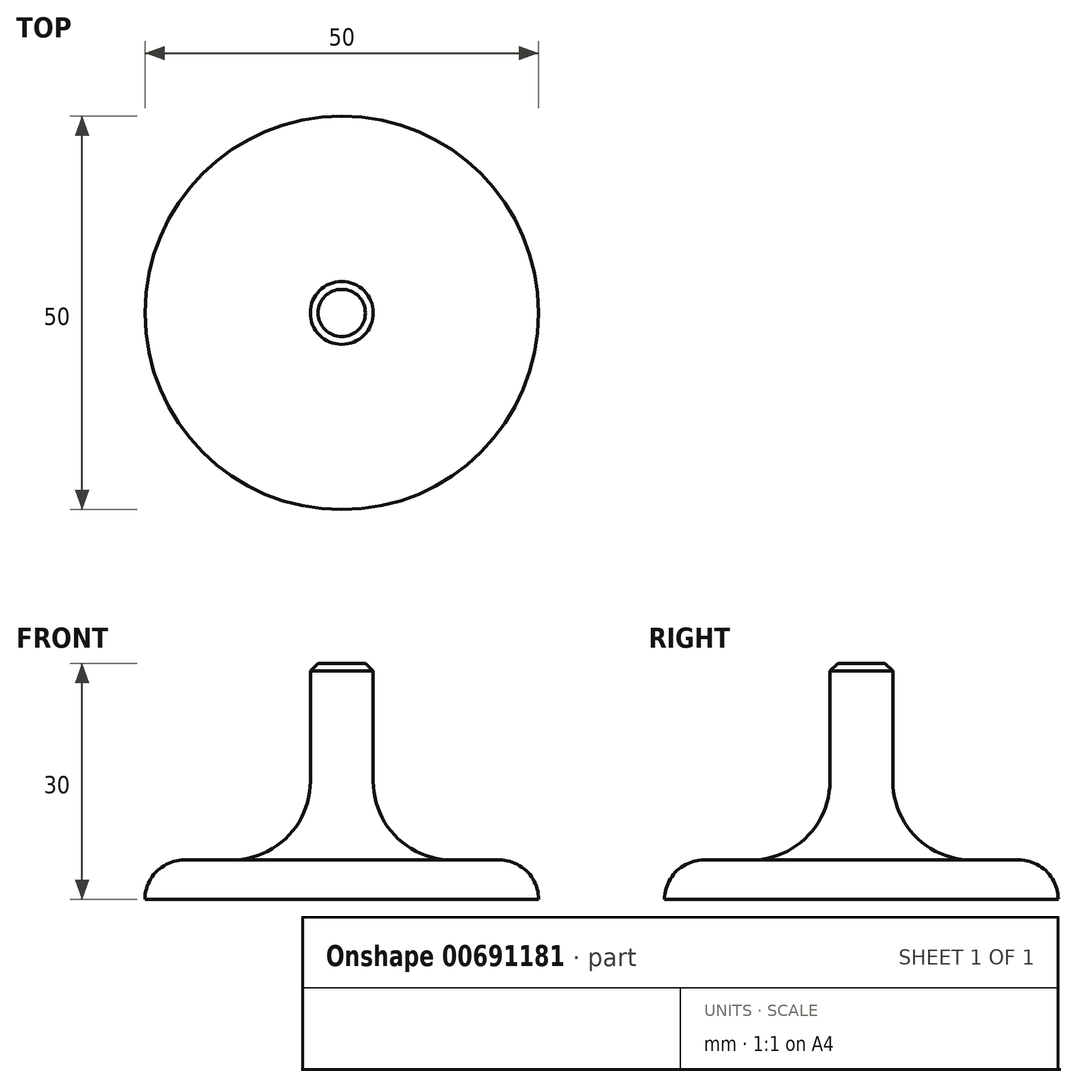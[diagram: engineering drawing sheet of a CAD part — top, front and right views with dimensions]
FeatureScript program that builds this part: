
annotation { "Feature Type Name" : "Feature", "Feature Type Description" : "" }
export const myFeature = defineFeature(function(context is Context, id is Id, definition is map)
    precondition{}
    {
        {
            var Q0;
            Q0=qCreatedBy(makeId("Top.planeOp"),FACE);
            var sketch = newSketch(context, id + "F0", { "sketchPlane" : qUnion([Q0])});
            skCircle(sketch, "E0", {"center": v(0, 0) * mm, "radius": 25 * mm});
            skSolve(sketch);
        }
        {
            var Q0;
            Q0=makeQuery(id+"F0.imprint","IMPRINT",FACE,{"disambiguationData":[TD([[makeQuery(id+"F0.imprint","IMPRINT",EDGE,{"derivedFrom":sQuery(id+"F0.wireOp",EDGE,"E0")}),1.0]])]});
            var sketch = newSketch(context, id + "F1", { "sketchPlane" : qUnion([Q0])});
            skCircle(sketch, "E1", {"center": v(0, 0) * mm, "radius": 4 * mm});
            skSolve(sketch);
        }
        {
            var Q0;
            Q0=makeQuery(id+"F0.imprint","IMPRINT",FACE,{"disambiguationData":[TD([[makeQuery(id+"F0.imprint","IMPRINT",EDGE,{"derivedFrom":sQuery(id+"F0.wireOp",EDGE,"E0")}),1.0]])]});
            extrude(context, id + "F2", {"entities" : qUnion([Q0]), "depth" : 5 * mm, "offsetDistance" : 25 * mm});
        }
        {
            var Q0;
            Q0=makeQuery(id+"F1.imprint","IMPRINT",FACE,{"disambiguationData":[TD([[makeQuery(id+"F1.imprint","IMPRINT",EDGE,{"derivedFrom":sQuery(id+"F1.wireOp",EDGE,"E1")}),1.0]])]});
            extrude(context, id + "F3", {"entities" : qUnion([Q0]), "operationType" : NewBodyOperationType.ADD, "depth" : 30 * mm, "offsetDistance" : 25 * mm});
        }
        {
            var Q0;
            Q0=makeQuery(id+"F3.boolean.opBoolean","INTERSECT",EDGE,{"derivedFrom":[makeQuery(id+"F2.opExtrude","CAP_FACE",FACE,{"disambiguationData":[OSD([sQuery(id+"F0.wireOp",EDGE,"E0")])],"isStart":false}),makeQuery(id+"F3.opExtrude","SWEPT_FACE",FACE,{"disambiguationData":[OSD([sQuery(id+"F1.wireOp",EDGE,"E1")])]})]});
            fillet(context, id + "F4", {"entities" : qUnion([Q0]), "radius" : 10 * mm, "tangentPropagation" : true, "allowEdgeOverflow" : false});
        }
        {
            var Q0;
            Q0=makeQuery(id+"F2.opExtrude","CAP_EDGE",EDGE,{"disambiguationData":[OSD([sQuery(id+"F0.wireOp",EDGE,"E0")])],"isStart":false});
            fillet(context, id + "F5", {"entities" : qUnion([Q0]), "radius" : 5 * mm, "tangentPropagation" : true, "allowEdgeOverflow" : false});
        }
        {
            var Q0;
            Q0=makeQuery(id+"F3.opExtrude","CAP_EDGE",EDGE,{"disambiguationData":[OSD([sQuery(id+"F1.wireOp",EDGE,"E1")])],"isStart":false});
            chamfer(context, id + "F6", {"entities" : qUnion([Q0]), "width" : 1 * mm, "tangentPropagation" : true});
        }
    });
